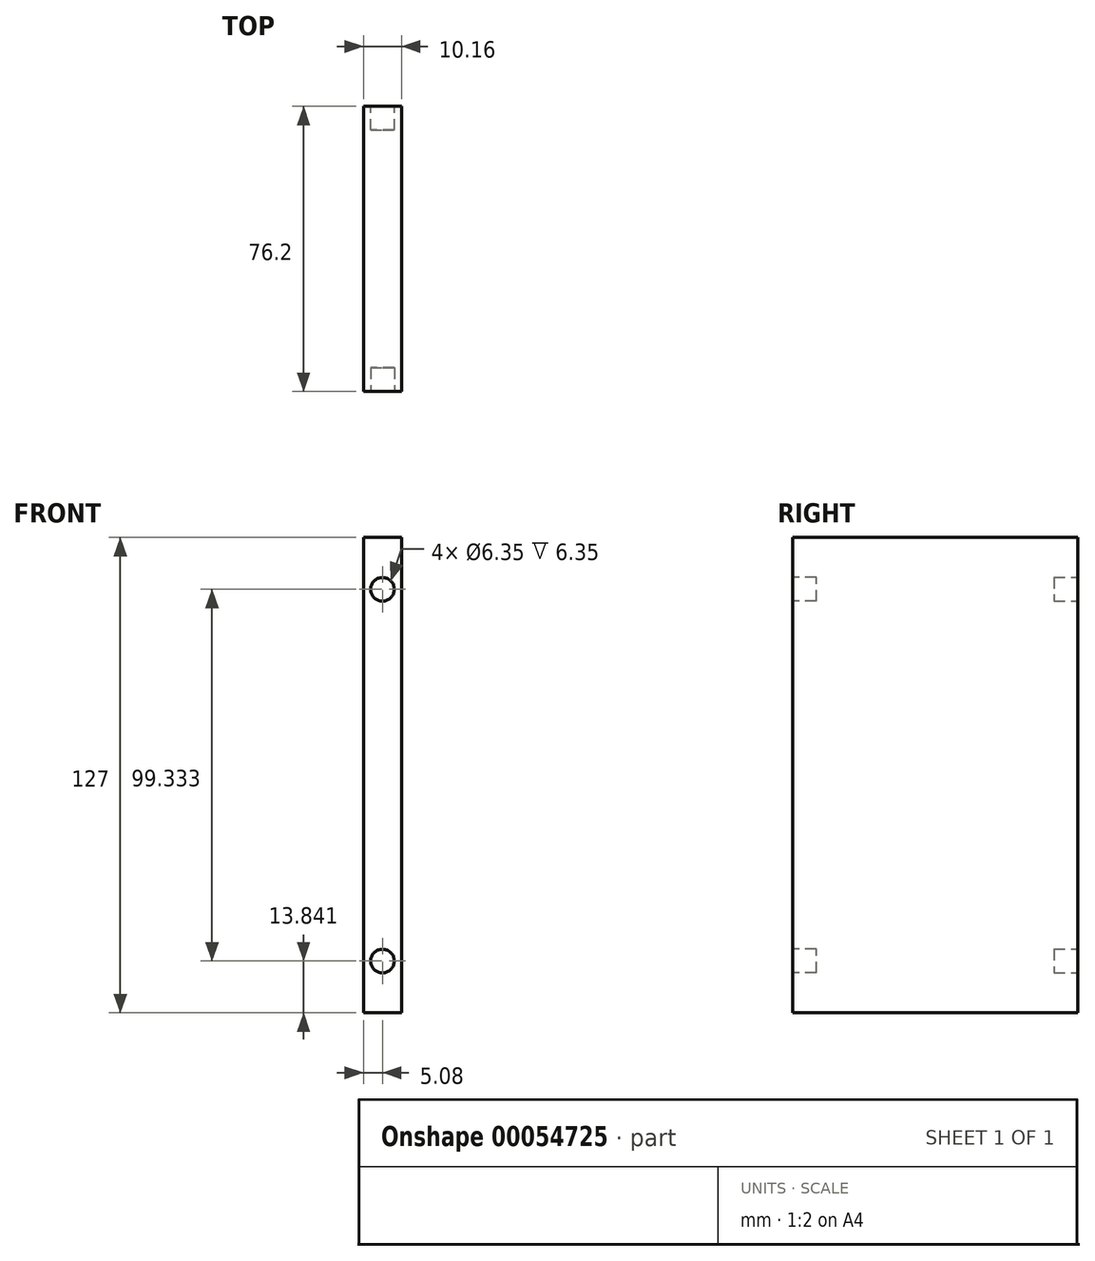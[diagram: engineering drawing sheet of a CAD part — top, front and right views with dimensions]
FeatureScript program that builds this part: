
annotation { "Feature Type Name" : "Feature", "Feature Type Description" : "" }
export const myFeature = defineFeature(function(context is Context, id is Id, definition is map)
    precondition{}
    {
        {
            var Q0;
            Q0=qCreatedBy(makeId("Right.planeOp"),FACE);
            var sketch = newSketch(context, id + "F0", { "sketchPlane" : qUnion([Q0])});
            skLineSegment(sketch, "E0.bottom", {"start": v(-40.53, 67.63) * mm, "end": v(35.67, 67.63) * mm});
            skLineSegment(sketch, "E0.top", {"start": v(-40.53, -59.37) * mm, "end": v(35.67, -59.37) * mm});
            skLineSegment(sketch, "E0.left", {"start": v(-40.53, 67.63) * mm, "end": v(-40.53, -59.37) * mm});
            skLineSegment(sketch, "E0.right", {"start": v(35.67, 67.63) * mm, "end": v(35.67, -59.37) * mm});
            skSolve(sketch);
        }
        {
            var Q0;
            Q0=makeQuery(id+"F0.imprint","IMPRINT",FACE,{"disambiguationData":[TD([[makeQuery(id+"F0.imprint","IMPRINT",EDGE,{"derivedFrom":sQuery(id+"F0.wireOp",EDGE,"E0.bottom")}),-1.0]])]});
            extrude(context, id + "F1", {"entities" : qUnion([Q0]), "depth" : 10.16 * mm});
        }
        {
            var Q0;
            Q0=makeQuery(id+"F1.opExtrude","SWEPT_FACE",FACE,{"disambiguationData":[OSD([sQuery(id+"F0.wireOp",EDGE,"E0.left")])]});
            var sketch = newSketch(context, id + "F2", { "sketchPlane" : qUnion([Q0])});
            skCircle(sketch, "E1", {"center": v(5.08, 53.79) * mm, "radius": 3.18 * mm});
            skPoint(sketch, "E1.centerSnap0", {"position": v(5.08, 67.63) * mm});
            skCircle(sketch, "E2", {"center": v(5.08, -45.53) * mm, "radius": 3.18 * mm});
            skPoint(sketch, "E2.centerSnap0", {"position": v(5.08, -59.37) * mm});
            skSolve(sketch);
        }
        {
            var Q0;
            Q0=makeQuery(id+"F2.imprint","IMPRINT",FACE,{"disambiguationData":[TD([[makeQuery(id+"F2.imprint","IMPRINT",EDGE,{"derivedFrom":sQuery(id+"F2.wireOp",EDGE,"E2")}),1.0]])]});
            extrude(context, id + "F3", {"entities" : qUnion([Q0]), "operationType" : NewBodyOperationType.REMOVE, "oppositeDirection" : true, "depth" : 6.35 * mm});
        }
        {
            var Q0;
            Q0=makeQuery(id+"F2.imprint","IMPRINT",FACE,{"disambiguationData":[TD([[makeQuery(id+"F2.imprint","IMPRINT",EDGE,{"derivedFrom":sQuery(id+"F2.wireOp",EDGE,"E1")}),1.0]])]});
            extrude(context, id + "F4", {"entities" : qUnion([Q0]), "operationType" : NewBodyOperationType.REMOVE, "oppositeDirection" : true, "depth" : 6.35 * mm});
        }
        {
            var Q0;
            Q0=makeQuery(id+"F1.opExtrude","SWEPT_FACE",FACE,{"disambiguationData":[OSD([sQuery(id+"F0.wireOp",EDGE,"E0.right")])]});
            var sketch = newSketch(context, id + "F5", { "sketchPlane" : qUnion([Q0])});
            skCircle(sketch, "E3", {"center": v(-5.08, 53.8) * mm, "radius": 3.18 * mm});
            skPoint(sketch, "E3.centerSnap0", {"position": v(-5.08, 67.63) * mm});
            skCircle(sketch, "E4", {"center": v(-5.08, -45.53) * mm, "radius": 3.18 * mm});
            skPoint(sketch, "E4.centerSnap0", {"position": v(-5.08, -59.37) * mm});
            skSolve(sketch);
        }
        {
            var Q0;
            Q0=makeQuery(id+"F5.imprint","IMPRINT",FACE,{"disambiguationData":[TD([[makeQuery(id+"F5.imprint","IMPRINT",EDGE,{"derivedFrom":sQuery(id+"F5.wireOp",EDGE,"E3")}),1.0]])]});
            var Q1;
            Q1=makeQuery(id+"F5.imprint","IMPRINT",FACE,{"disambiguationData":[TD([[makeQuery(id+"F5.imprint","IMPRINT",EDGE,{"derivedFrom":sQuery(id+"F5.wireOp",EDGE,"E4")}),1.0]])]});
            extrude(context, id + "F6", {"entities" : qUnion([Q0, Q1]), "operationType" : NewBodyOperationType.REMOVE, "oppositeDirection" : true, "depth" : 6.35 * mm});
        }
    });
